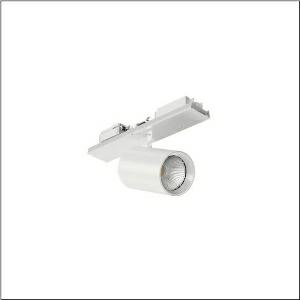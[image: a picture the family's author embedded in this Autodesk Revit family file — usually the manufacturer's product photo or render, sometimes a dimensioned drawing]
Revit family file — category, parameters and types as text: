
# Revit family: licross_r__spot_31_51sl12da33b_14a7
name_source: partatom
category: Lighting Fixtures
units: mm (PartAtom-declared; Revit-internal decimal feet)

## family parameters
Cut with Voids When Loaded = No
Host = Face
Light Source = No
Part Type = Normal
Room Calculation Point = No
Round Connector Dimension = Use Diameter
Shared = No

## types (1)
- --- (1 x LED, 3540 lm, 28.6 W, 3000K)
    Apparent Load = 29 VA
    CIE Flux Codes = 93 97 99 100 100
    Color Rendering = 90
    Color Temperature = 3000K
    Default Elevation = 1800 mm
    Description = Licross® Spot 31, directional spotlight, light control with lens, of plastic, LED rated luminous flux: 3.540lm, light colour: 930, with plug, 5-pole, mains connection: 220..240V, AC, 50/60Hz, of aluminium, traffic white (RAL 9016), length: 300mm, diameter: 90mm, protection rating (complete): IP20, insulation class (complete): insulation class I (protective earthing), certification: CE, packaging unit: 1 piece
    Height = 175 mm
    Lamp = 1 x LED
    Lamp Light Flux = 3540 lm
    Lamp Power = 28.6 W
    Lamp count = 1
    Length = 90 mm
    Luminous efficacy = 124 lm/W
    Manufacturer = Siteco
    ModVariant = No
    Model = 51SL12DA33B
    Mounting Place = Ceiling
    Mounting Type = Pendant
    Number of Poles = 1
    OnlyDefault = Yes
    Power Factor = 1
    Product Name = Licross® Spot 31
    Product group = directional spotlight
    ProductGroupID = 905
    Protection Class = Protection class I
    Protection Degree = IP 20
    RLX_Detail_Level = 1
    RLX_Emergency_Light_Flux = 0 lm
    RLX_Emergency_Type = 0
    RLX_Emergency_Type_DB = No
    RlxData = <blob elided: 14801 chars, md5=18d6db9d>
    Socket = socket
    Standby Power = 0 W
    System Light Flux = 3540 lm
    System Power = 29 W
    Type Comments = factory setting: luminous flux: 100 % | (ON | ON | ON) | 700 mA
    Type Image = l_1245720.jpg
    URL = http://relux.com
    VarID = @adj_154111
    Voltage = 0 V
    Weight = 0.00 kg
    Width = 0 mm  [stored 0 ft]

note: [stored X ft] marks values corroborated as IEEE doubles in the binary element streams (Revit-internal decimal feet)

## geometry (parser evidence)
native form markers: Sweep x13
no freeform markers — native parametric forms only
